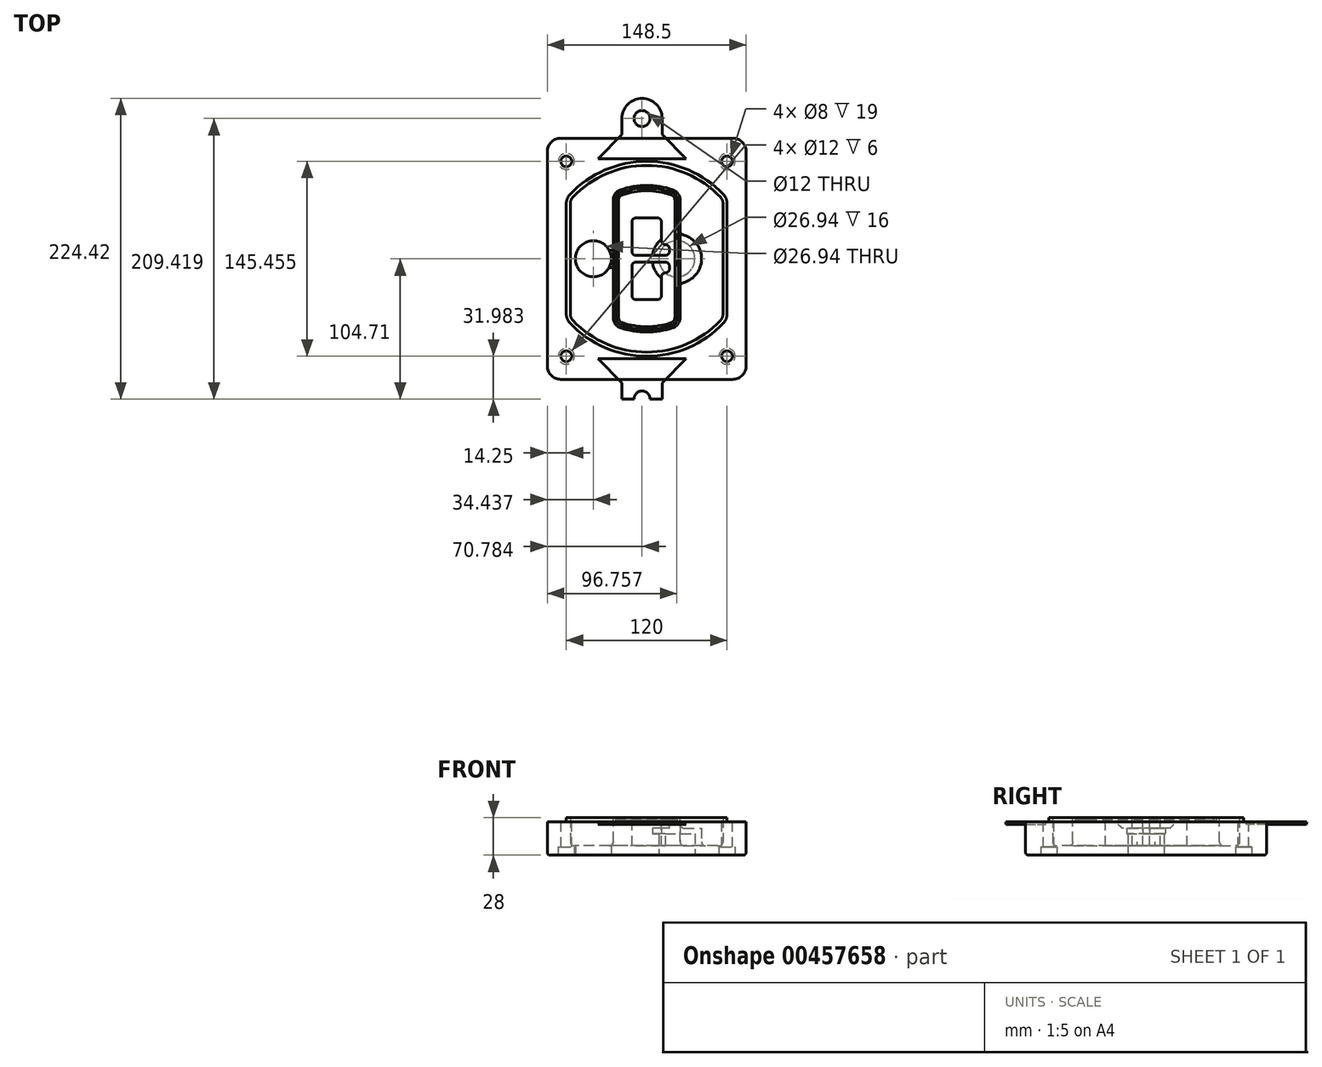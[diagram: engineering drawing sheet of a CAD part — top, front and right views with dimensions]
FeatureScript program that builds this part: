
annotation { "Feature Type Name" : "Feature", "Feature Type Description" : "" }
export const myFeature = defineFeature(function(context is Context, id is Id, definition is map)
    precondition{}
    {
        {
            var Q0;
            Q0=qCreatedBy(makeId("Top.planeOp"),FACE);
            var sketch = newSketch(context, id + "F0", { "sketchPlane" : qUnion([Q0])});
            skPoint(sketch, "E0.rect.middle", {"position": v(0, 0) * mm});
            skLineSegment(sketch, "E1.bottom", {"start": v(-64.25, -90) * mm, "end": v(64.25, -90) * mm});
            skLineSegment(sketch, "E1.top", {"start": v(-64.25, 90) * mm, "end": v(64.25, 90) * mm});
            skLineSegment(sketch, "E1.left", {"start": v(-74.25, -80) * mm, "end": v(-74.25, 80) * mm});
            skLineSegment(sketch, "E1.right", {"start": v(74.25, -80) * mm, "end": v(74.25, 80) * mm});
            skLineSegment(sketch, "E2", {"start": v(-74.25, 90) * mm, "end": v(74.25, -90) * mm, "construction": true});
            skLineSegment(sketch, "E3", {"start": v(74.25, 90) * mm, "end": v(-74.25, -90) * mm, "construction": true});
            skCircle(sketch, "E4", {"center": v(-60, 72.73) * mm, "radius": 4 * mm});
            skCircle(sketch, "E5", {"center": v(60, 72.73) * mm, "radius": 4 * mm});
            skCircle(sketch, "E6", {"center": v(60, -72.73) * mm, "radius": 4 * mm});
            skCircle(sketch, "E7", {"center": v(-60, -72.73) * mm, "radius": 4 * mm});
            skLineSegment(sketch, "E8", {"start": v(-60, 72.73) * mm, "end": v(60, 72.73) * mm, "construction": true});
            skLineSegment(sketch, "E9", {"start": v(60, 72.73) * mm, "end": v(60, -72.73) * mm, "construction": true});
            skLineSegment(sketch, "E10", {"start": v(60, -72.73) * mm, "end": v(-60, -72.73) * mm, "construction": true});
            skLineSegment(sketch, "E11", {"start": v(-60, -72.73) * mm, "end": v(-60, 72.73) * mm, "construction": true});
            skLineSegment(sketch, "E12", {"start": v(-60, 41.18) * mm, "end": v(-60, -41.18) * mm});
            skLineSegment(sketch, "E13", {"start": v(60, 41.18) * mm, "end": v(60, -41.18) * mm});
            skArc(sketch, "E14", {"start": v(57.27, 48.05) * mm, "mid": v(0, 72.73) * mm, "end": v(-57.27, 48.05) * mm});
            skArc(sketch, "E15", {"start": v(-57.27, -48.05) * mm, "mid": v(0, -72.73) * mm, "end": v(57.27, -48.05) * mm});
            skLineSegment(sketch, "E16", {"start": v(-60, 0) * mm, "end": v(60, 0) * mm, "construction": true});
            skPoint(sketch, "E17.visualSharp", {"position": v(-60, -45) * mm});
            skArc(sketch, "E17.filletArc", {"start": v(-60, -41.18) * mm, "mid": v(-59.3, -44.87) * mm, "end": v(-57.27, -48.05) * mm});
            skPoint(sketch, "E18.visualSharp", {"position": v(-60, 45) * mm});
            skArc(sketch, "E18.filletArc", {"start": v(-57.27, 48.05) * mm, "mid": v(-59.3, 44.87) * mm, "end": v(-60, 41.18) * mm});
            skPoint(sketch, "E19.visualSharp", {"position": v(60, 45) * mm});
            skArc(sketch, "E19.filletArc", {"start": v(60, 41.18) * mm, "mid": v(59.3, 44.87) * mm, "end": v(57.27, 48.05) * mm});
            skPoint(sketch, "E20.visualSharp", {"position": v(60, -45) * mm});
            skArc(sketch, "E20.filletArc", {"start": v(57.27, -48.05) * mm, "mid": v(59.3, -44.87) * mm, "end": v(60, -41.18) * mm});
            skPoint(sketch, "E21.visualSharp", {"position": v(-74.25, 90) * mm});
            skArc(sketch, "E21.filletArc", {"start": v(-64.25, 90) * mm, "mid": v(-71.32, 87.07) * mm, "end": v(-74.25, 80) * mm});
            skPoint(sketch, "E22.visualSharp", {"position": v(74.25, 90) * mm});
            skArc(sketch, "E22.filletArc", {"start": v(74.25, 80) * mm, "mid": v(71.32, 87.07) * mm, "end": v(64.25, 90) * mm});
            skPoint(sketch, "E23.visualSharp", {"position": v(74.25, -90) * mm});
            skArc(sketch, "E23.filletArc", {"start": v(64.25, -90) * mm, "mid": v(71.32, -87.07) * mm, "end": v(74.25, -80) * mm});
            skPoint(sketch, "E24.visualSharp", {"position": v(-74.25, -90) * mm});
            skArc(sketch, "E24.filletArc", {"start": v(-74.25, -80) * mm, "mid": v(-71.32, -87.07) * mm, "end": v(-64.25, -90) * mm});
            skArc(sketch, "E25.0", {"start": v(57, 41.18) * mm, "mid": v(56.5, 43.76) * mm, "end": v(55.09, 45.99) * mm});
            skLineSegment(sketch, "E25.1", {"start": v(57, 41.18) * mm, "end": v(57, -41.18) * mm});
            skArc(sketch, "E25.2", {"start": v(55.09, -45.99) * mm, "mid": v(56.5, -43.76) * mm, "end": v(57, -41.18) * mm});
            skArc(sketch, "E25.3", {"start": v(-55.09, -45.99) * mm, "mid": v(0, -69.73) * mm, "end": v(55.09, -45.99) * mm});
            skArc(sketch, "E25.4", {"start": v(-57, -41.18) * mm, "mid": v(-56.5, -43.76) * mm, "end": v(-55.09, -45.99) * mm});
            skArc(sketch, "E25.5", {"start": v(55.09, 45.99) * mm, "mid": v(0, 69.73) * mm, "end": v(-55.09, 45.99) * mm});
            skLineSegment(sketch, "E25.6", {"start": v(-57, 41.18) * mm, "end": v(-57, -41.18) * mm});
            skArc(sketch, "E25.7", {"start": v(-55.09, 45.99) * mm, "mid": v(-56.5, 43.76) * mm, "end": v(-57, 41.18) * mm});
            skArc(sketch, "E26.0", {"start": v(-60.18, 50.8) * mm, "mid": v(-63, 46.35) * mm, "end": v(-64, 41.18) * mm});
            skArc(sketch, "E26.1", {"start": v(60.18, 50.8) * mm, "mid": v(0, 76.73) * mm, "end": v(-60.18, 50.8) * mm});
            skArc(sketch, "E26.2", {"start": v(64, 41.18) * mm, "mid": v(63, 46.35) * mm, "end": v(60.18, 50.8) * mm});
            skLineSegment(sketch, "E26.3", {"start": v(64, 41.18) * mm, "end": v(64, -41.18) * mm});
            skArc(sketch, "E26.4", {"start": v(60.18, -50.8) * mm, "mid": v(63, -46.35) * mm, "end": v(64, -41.18) * mm});
            skLineSegment(sketch, "E26.5", {"start": v(-64, 41.18) * mm, "end": v(-64, -41.18) * mm});
            skArc(sketch, "E26.6", {"start": v(-60.18, -50.8) * mm, "mid": v(0, -76.73) * mm, "end": v(60.18, -50.8) * mm});
            skArc(sketch, "E26.7", {"start": v(-64, -41.18) * mm, "mid": v(-63, -46.35) * mm, "end": v(-60.18, -50.8) * mm});
            skSolve(sketch);
        }
        {
            var Q0;
            Q0=makeQuery(id+"F0.imprint","IMPRINT",FACE,{"disambiguationData":[TD([[makeQuery(id+"F0.imprint","IMPRINT",EDGE,{"derivedFrom":sQuery(id+"F0.wireOp",EDGE,"E1.bottom")}),1.0]])]});
            var Q1;
            Q1=makeQuery(id+"F0.imprint","IMPRINT",FACE,{"disambiguationData":[TD([[makeQuery(id+"F0.imprint","IMPRINT",EDGE,{"derivedFrom":sQuery(id+"F0.wireOp",EDGE,"E12")}),1.0]])]});
            var Q2;
            Q2=makeQuery(id+"F0.imprint","IMPRINT",FACE,{"disambiguationData":[TD([[makeQuery(id+"F0.imprint","IMPRINT",EDGE,{"derivedFrom":sQuery(id+"F0.wireOp",EDGE,"E25.0")}),1.0]])]});
            var Q3;
            Q3=makeQuery(id+"F0.imprint","IMPRINT",FACE,{"disambiguationData":[TD([[makeQuery(id+"F0.imprint","IMPRINT",EDGE,{"derivedFrom":sQuery(id+"F0.wireOp",EDGE,"E12")}),-1.0]])]});
            extrude(context, id + "F1", {"entities" : qUnion([Q0, Q1, Q2, Q3]), "oppositeDirection" : true, "depth" : 25 * mm});
        }
        {
            var Q0;
            Q0=makeQuery(id+"F0.imprint","IMPRINT",FACE,{"disambiguationData":[TD([[makeQuery(id+"F0.imprint","IMPRINT",EDGE,{"derivedFrom":sQuery(id+"F0.wireOp",EDGE,"E12")}),1.0]])]});
            extrude(context, id + "F2", {"entities" : qUnion([Q0]), "operationType" : NewBodyOperationType.ADD, "depth" : 3 * mm});
        }
        {
            var Q0;
            Q0=makeQuery(id+"F0.imprint","IMPRINT",FACE,{"disambiguationData":[TD([[makeQuery(id+"F0.imprint","IMPRINT",EDGE,{"derivedFrom":sQuery(id+"F0.wireOp",EDGE,"E25.0")}),1.0]])]});
            extrude(context, id + "F3", {"entities" : qUnion([Q0]), "operationType" : NewBodyOperationType.REMOVE, "oppositeDirection" : true, "depth" : 18 * mm});
        }
        {
            var Q0;
            Q0=makeQuery(id+"F2.opExtrude","CAP_FACE",FACE,{"disambiguationData":[OSD([sQuery(id+"F0.wireOp",EDGE,"E12"),sQuery(id+"F0.wireOp",EDGE,"E13"),sQuery(id+"F0.wireOp",EDGE,"E14"),sQuery(id+"F0.wireOp",EDGE,"E15"),sQuery(id+"F0.wireOp",EDGE,"E17.filletArc"),sQuery(id+"F0.wireOp",EDGE,"E18.filletArc"),sQuery(id+"F0.wireOp",EDGE,"E19.filletArc"),sQuery(id+"F0.wireOp",EDGE,"E20.filletArc"),sQuery(id+"F0.wireOp",EDGE,"E25.0"),sQuery(id+"F0.wireOp",EDGE,"E25.1"),sQuery(id+"F0.wireOp",EDGE,"E25.2"),sQuery(id+"F0.wireOp",EDGE,"E25.3"),sQuery(id+"F0.wireOp",EDGE,"E25.4"),sQuery(id+"F0.wireOp",EDGE,"E25.5"),sQuery(id+"F0.wireOp",EDGE,"E25.6"),sQuery(id+"F0.wireOp",EDGE,"E25.7")])],"isStart":false});
            var sketch = newSketch(context, id + "F4", { "sketchPlane" : qUnion([Q0])});
            skArc(sketch, "E27.0", {"start": v(-19.58, -51.49) * mm, "mid": v(0, -54.73) * mm, "end": v(19.58, -51.49) * mm});
            skArc(sketch, "E28.0", {"start": v(19.58, 51.49) * mm, "mid": v(0, 54.73) * mm, "end": v(-19.58, 51.49) * mm});
            skLineSegment(sketch, "E29", {"start": v(-25, 43.91) * mm, "end": v(-25, -43.91) * mm});
            skLineSegment(sketch, "E30", {"start": v(25, 43.91) * mm, "end": v(25, -43.91) * mm});
            skLineSegment(sketch, "E31", {"start": v(-25, 49.35) * mm, "end": v(25, 49.35) * mm, "construction": true});
            skLineSegment(sketch, "E32", {"start": v(-25, -49.35) * mm, "end": v(25, -49.35) * mm, "construction": true});
            skPoint(sketch, "E33.visualSharp", {"position": v(-25, 49.35) * mm});
            skArc(sketch, "E33.filletArc", {"start": v(-19.58, 51.49) * mm, "mid": v(-23.5, 48.57) * mm, "end": v(-25, 43.91) * mm});
            skPoint(sketch, "E34.visualSharp", {"position": v(25, 49.35) * mm});
            skArc(sketch, "E34.filletArc", {"start": v(25, 43.91) * mm, "mid": v(23.5, 48.57) * mm, "end": v(19.58, 51.49) * mm});
            skPoint(sketch, "E35.visualSharp", {"position": v(25, -49.35) * mm});
            skArc(sketch, "E35.filletArc", {"start": v(19.58, -51.49) * mm, "mid": v(23.5, -48.57) * mm, "end": v(25, -43.91) * mm});
            skPoint(sketch, "E36.visualSharp", {"position": v(-25, -49.35) * mm});
            skArc(sketch, "E36.filletArc", {"start": v(-25, -43.91) * mm, "mid": v(-23.5, -48.57) * mm, "end": v(-19.58, -51.49) * mm});
            skArc(sketch, "E37.0", {"start": v(55.09, 45.99) * mm, "mid": v(0, 69.73) * mm, "end": v(-55.09, 45.99) * mm});
            skArc(sketch, "E37.1", {"start": v(-55.09, 45.99) * mm, "mid": v(-56.5, 43.76) * mm, "end": v(-57, 41.18) * mm});
            skLineSegment(sketch, "E37.2", {"start": v(-57, 41.18) * mm, "end": v(-57, -41.18) * mm});
            skArc(sketch, "E37.3", {"start": v(-57, -41.18) * mm, "mid": v(-56.5, -43.76) * mm, "end": v(-55.09, -45.99) * mm});
            skArc(sketch, "E37.4", {"start": v(-55.09, -45.99) * mm, "mid": v(0, -69.73) * mm, "end": v(55.09, -45.99) * mm});
            skArc(sketch, "E37.5", {"start": v(55.09, -45.99) * mm, "mid": v(56.5, -43.76) * mm, "end": v(57, -41.18) * mm});
            skLineSegment(sketch, "E37.6", {"start": v(57, 41.18) * mm, "end": v(57, -41.18) * mm});
            skArc(sketch, "E37.7", {"start": v(57, 41.18) * mm, "mid": v(56.5, 43.76) * mm, "end": v(55.09, 45.99) * mm});
            skLineSegment(sketch, "E38.0", {"start": v(23, 43.91) * mm, "end": v(23, -43.91) * mm});
            skArc(sketch, "E38.1", {"start": v(18.93, -49.6) * mm, "mid": v(21.88, -47.4) * mm, "end": v(23, -43.91) * mm});
            skArc(sketch, "E38.2", {"start": v(-18.93, -49.6) * mm, "mid": v(0, -52.73) * mm, "end": v(18.93, -49.6) * mm});
            skArc(sketch, "E38.3", {"start": v(-23, -43.91) * mm, "mid": v(-21.88, -47.4) * mm, "end": v(-18.93, -49.6) * mm});
            skLineSegment(sketch, "E38.4", {"start": v(-23, 43.91) * mm, "end": v(-23, -43.91) * mm});
            skArc(sketch, "E38.5", {"start": v(23, 43.91) * mm, "mid": v(21.88, 47.4) * mm, "end": v(18.93, 49.6) * mm});
            skArc(sketch, "E38.6", {"start": v(-18.93, 49.6) * mm, "mid": v(-21.88, 47.4) * mm, "end": v(-23, 43.91) * mm});
            skArc(sketch, "E38.7", {"start": v(18.93, 49.6) * mm, "mid": v(0, 52.73) * mm, "end": v(-18.93, 49.6) * mm});
            skArc(sketch, "E39.0", {"start": v(21, 43.91) * mm, "mid": v(20.25, 46.24) * mm, "end": v(18.29, 47.7) * mm});
            skLineSegment(sketch, "E39.1", {"start": v(21, 43.91) * mm, "end": v(21, -43.91) * mm});
            skArc(sketch, "E39.2", {"start": v(18.29, -47.7) * mm, "mid": v(20.25, -46.24) * mm, "end": v(21, -43.91) * mm});
            skArc(sketch, "E39.3", {"start": v(-18.29, -47.7) * mm, "mid": v(0, -50.73) * mm, "end": v(18.29, -47.7) * mm});
            skArc(sketch, "E39.4", {"start": v(-21, -43.91) * mm, "mid": v(-20.25, -46.24) * mm, "end": v(-18.29, -47.7) * mm});
            skArc(sketch, "E39.5", {"start": v(18.29, 47.7) * mm, "mid": v(0, 50.73) * mm, "end": v(-18.29, 47.7) * mm});
            skLineSegment(sketch, "E39.6", {"start": v(-21, 43.91) * mm, "end": v(-21, -43.91) * mm});
            skArc(sketch, "E39.7", {"start": v(-18.29, 47.7) * mm, "mid": v(-20.25, 46.24) * mm, "end": v(-21, 43.91) * mm});
            skLineSegment(sketch, "E40", {"start": v(-25, 0) * mm, "end": v(25, 0) * mm, "construction": true});
            skLineSegment(sketch, "E41", {"start": v(-11, 5.5) * mm, "end": v(-11, 27.5) * mm});
            skLineSegment(sketch, "E42", {"start": v(-8, 30.5) * mm, "end": v(8, 30.5) * mm});
            skLineSegment(sketch, "E43", {"start": v(11, 27.5) * mm, "end": v(11, 13.5) * mm});
            skLineSegment(sketch, "E44", {"start": v(14, 10.5) * mm, "end": v(14, 10.5) * mm});
            skLineSegment(sketch, "E45", {"start": v(17, 7.5) * mm, "end": v(17, 5.5) * mm});
            skLineSegment(sketch, "E46", {"start": v(14, 2.5) * mm, "end": v(-8, 2.5) * mm});
            skPoint(sketch, "E47.visualSharp", {"position": v(-11, 30.5) * mm});
            skArc(sketch, "E47.filletArc", {"start": v(-8, 30.5) * mm, "mid": v(-10.12, 29.62) * mm, "end": v(-11, 27.5) * mm});
            skPoint(sketch, "E48.visualSharp", {"position": v(11, 30.5) * mm});
            skArc(sketch, "E48.filletArc", {"start": v(11, 27.5) * mm, "mid": v(10.12, 29.62) * mm, "end": v(8, 30.5) * mm});
            skPoint(sketch, "E49.visualSharp", {"position": v(11, 10.5) * mm});
            skArc(sketch, "E49.filletArc", {"start": v(11, 13.5) * mm, "mid": v(11.88, 11.38) * mm, "end": v(14, 10.5) * mm});
            skPoint(sketch, "E50.visualSharp", {"position": v(17, 10.5) * mm});
            skArc(sketch, "E50.filletArc", {"start": v(17, 7.5) * mm, "mid": v(16.12, 9.62) * mm, "end": v(14, 10.5) * mm});
            skPoint(sketch, "E51.visualSharp", {"position": v(17, 2.5) * mm});
            skArc(sketch, "E51.filletArc", {"start": v(14, 2.5) * mm, "mid": v(16.12, 3.38) * mm, "end": v(17, 5.5) * mm});
            skPoint(sketch, "E52.visualSharp", {"position": v(-11, 2.5) * mm});
            skArc(sketch, "E52.filletArc", {"start": v(-11, 5.5) * mm, "mid": v(-10.12, 3.38) * mm, "end": v(-8, 2.5) * mm});
            skLineSegment(sketch, "E53.0.MirrorCS", {"start": v(14, -2.5) * mm, "end": v(-8, -2.5) * mm});
            skArc(sketch, "E54.0.MirrorCS", {"start": v(-11, -5.5) * mm, "mid": v(-10.12, -3.38) * mm, "end": v(-8, -2.5) * mm});
            skLineSegment(sketch, "E55.0.MirrorCS", {"start": v(-11, -5.5) * mm, "end": v(-11, -27.5) * mm});
            skArc(sketch, "E56.0.MirrorCS", {"start": v(-8, -30.5) * mm, "mid": v(-10.12, -29.62) * mm, "end": v(-11, -27.5) * mm});
            skLineSegment(sketch, "E57.0.MirrorCS", {"start": v(-8, -30.5) * mm, "end": v(8, -30.5) * mm});
            skArc(sketch, "E58.0.MirrorCS", {"start": v(11, -27.5) * mm, "mid": v(10.12, -29.62) * mm, "end": v(8, -30.5) * mm});
            skLineSegment(sketch, "E59.0.MirrorCS", {"start": v(11, -27.5) * mm, "end": v(11, -13.5) * mm});
            skArc(sketch, "E60.0.MirrorCS", {"start": v(11, -13.5) * mm, "mid": v(11.88, -11.38) * mm, "end": v(14, -10.5) * mm});
            skArc(sketch, "E61.0.MirrorCS", {"start": v(17, -7.5) * mm, "mid": v(16.12, -9.62) * mm, "end": v(14, -10.5) * mm});
            skLineSegment(sketch, "E62.0.MirrorCS", {"start": v(17, -7.5) * mm, "end": v(17, -5.5) * mm});
            skArc(sketch, "E63.0.MirrorCS", {"start": v(14, -2.5) * mm, "mid": v(16.12, -3.38) * mm, "end": v(17, -5.5) * mm});
            skSolve(sketch);
        }
        {
            var Q0;
            Q0=makeQuery(id+"F4.imprint","IMPRINT",FACE,{"disambiguationData":[TD([[makeQuery(id+"F4.imprint","IMPRINT",EDGE,{"derivedFrom":sQuery(id+"F4.wireOp",EDGE,"E27.0")}),1.0]])]});
            var Q1;
            Q1=makeQuery(id+"F4.imprint","IMPRINT",FACE,{"disambiguationData":[TD([[makeQuery(id+"F4.imprint","IMPRINT",EDGE,{"derivedFrom":sQuery(id+"F4.wireOp",EDGE,"E38.0")}),-1.0]])]});
            var Q2;
            Q2=makeQuery(id+"F4.imprint","IMPRINT",FACE,{"disambiguationData":[TD([[makeQuery(id+"F4.imprint","IMPRINT",EDGE,{"derivedFrom":sQuery(id+"F4.wireOp",EDGE,"E39.0")}),1.0]])]});
            extrude(context, id + "F5", {"entities" : qUnion([Q0, Q1, Q2]), "operationType" : NewBodyOperationType.ADD, "endBound" : BoundingType.UP_TO_NEXT, "oppositeDirection" : true, "depth" : 25 * mm});
        }
        {
            var Q0;
            Q0=makeQuery(id+"F4.imprint","IMPRINT",FACE,{"disambiguationData":[TD([[makeQuery(id+"F4.imprint","IMPRINT",EDGE,{"derivedFrom":sQuery(id+"F4.wireOp",EDGE,"E38.0")}),-1.0]])]});
            extrude(context, id + "F6", {"entities" : qUnion([Q0]), "operationType" : NewBodyOperationType.REMOVE, "oppositeDirection" : true, "depth" : 2 * mm});
        }
        {
            var Q0;
            Q0=makeQuery(id+"F1.opExtrude","CAP_FACE",FACE,{"disambiguationData":[OSD([sQuery(id+"F0.wireOp",EDGE,"E1.bottom"),sQuery(id+"F0.wireOp",EDGE,"E1.top"),sQuery(id+"F0.wireOp",EDGE,"E1.left"),sQuery(id+"F0.wireOp",EDGE,"E1.right"),sQuery(id+"F0.wireOp",EDGE,"E4"),sQuery(id+"F0.wireOp",EDGE,"E5"),sQuery(id+"F0.wireOp",EDGE,"E6"),sQuery(id+"F0.wireOp",EDGE,"E7"),sQuery(id+"F0.wireOp",EDGE,"E21.filletArc"),sQuery(id+"F0.wireOp",EDGE,"E22.filletArc"),sQuery(id+"F0.wireOp",EDGE,"E23.filletArc"),sQuery(id+"F0.wireOp",EDGE,"E24.filletArc")])],"isStart":false});
            var sketch = newSketch(context, id + "F7", { "sketchPlane" : qUnion([Q0])});
            skCircle(sketch, "E64", {"center": v(22.5, 0) * mm, "radius": 13.47 * mm});
            skCircle(sketch, "E65", {"center": v(-39.81, 0) * mm, "radius": 13.47 * mm});
            skLineSegment(sketch, "E66", {"start": v(74.25, 0) * mm, "end": v(-74.25, 0) * mm});
            skCircle(sketch, "E67", {"center": v(22.5, 0) * mm, "radius": 18.47 * mm});
            skCircle(sketch, "E68", {"center": v(60, -72.73) * mm, "radius": 6 * mm});
            skCircle(sketch, "E69", {"center": v(-60, -72.73) * mm, "radius": 6 * mm});
            skCircle(sketch, "E70", {"center": v(-60, 72.73) * mm, "radius": 6 * mm});
            skCircle(sketch, "E71", {"center": v(60, 72.73) * mm, "radius": 6 * mm});
            skSolve(sketch);
        }
        {
            var Q0;
            {var subQ1=sQuery(id+"F7.wireOp",EDGE,"E66");var subQ4=sQuery(id+"F7.wireOp",EDGE,"E64");var subQ6=makeQuery(id+"F7.imprint","INTERSECT",VERTEX,{"disambiguationData":[OD(0.0)],"derivedFrom":[subQ4,subQ1]});Q0=makeQuery(id+"F7.imprint","IMPRINT",FACE,{"disambiguationData":[TD([[makeQuery(id+"F7.imprint","IMPRINT",EDGE,{"disambiguationData":[TD([[subQ6,-1.0]])],"derivedFrom":subQ4}),-1.0]])]});}
            var Q1;
            {var subQ0=sQuery(id+"F7.wireOp",EDGE,"E66");var subQ1=sQuery(id+"F7.wireOp",EDGE,"E64");var subQ3=makeQuery(id+"F7.imprint","INTERSECT",VERTEX,{"disambiguationData":[OD(0.0)],"derivedFrom":[subQ1,subQ0]});Q1=makeQuery(id+"F7.imprint","IMPRINT",FACE,{"disambiguationData":[TD([[makeQuery(id+"F7.imprint","IMPRINT",EDGE,{"disambiguationData":[TD([[subQ3,-1.0]])],"derivedFrom":subQ1}),1.0]])]});}
            var Q2;
            {var subQ0=sQuery(id+"F7.wireOp",EDGE,"E66");var subQ1=sQuery(id+"F7.wireOp",EDGE,"E64");var subQ3=makeQuery(id+"F7.imprint","INTERSECT",VERTEX,{"disambiguationData":[OD(0.0)],"derivedFrom":[subQ1,subQ0]});Q2=makeQuery(id+"F7.imprint","IMPRINT",FACE,{"disambiguationData":[TD([[makeQuery(id+"F7.imprint","IMPRINT",EDGE,{"disambiguationData":[TD([[subQ3,1.0]])],"derivedFrom":subQ1}),1.0]])]});}
            var Q3;
            {var subQ1=sQuery(id+"F7.wireOp",EDGE,"E66");var subQ4=sQuery(id+"F7.wireOp",EDGE,"E64");var subQ6=makeQuery(id+"F7.imprint","INTERSECT",VERTEX,{"disambiguationData":[OD(0.0)],"derivedFrom":[subQ4,subQ1]});Q3=makeQuery(id+"F7.imprint","IMPRINT",FACE,{"disambiguationData":[TD([[makeQuery(id+"F7.imprint","IMPRINT",EDGE,{"disambiguationData":[TD([[subQ6,1.0]])],"derivedFrom":subQ4}),-1.0]])]});}
            extrude(context, id + "F8", {"entities" : qUnion([Q0, Q1, Q2, Q3]), "operationType" : NewBodyOperationType.ADD, "oppositeDirection" : true, "depth" : 20 * mm});
        }
        {
            var Q0;
            {var subQ0=sQuery(id+"F7.wireOp",EDGE,"E66");var subQ1=sQuery(id+"F7.wireOp",EDGE,"E64");var subQ3=makeQuery(id+"F7.imprint","INTERSECT",VERTEX,{"disambiguationData":[OD(0.0)],"derivedFrom":[subQ1,subQ0]});Q0=makeQuery(id+"F7.imprint","IMPRINT",FACE,{"disambiguationData":[TD([[makeQuery(id+"F7.imprint","IMPRINT",EDGE,{"disambiguationData":[TD([[subQ3,-1.0]])],"derivedFrom":subQ1}),1.0]])]});}
            var Q1;
            {var subQ0=sQuery(id+"F7.wireOp",EDGE,"E66");var subQ1=sQuery(id+"F7.wireOp",EDGE,"E64");var subQ3=makeQuery(id+"F7.imprint","INTERSECT",VERTEX,{"disambiguationData":[OD(0.0)],"derivedFrom":[subQ1,subQ0]});Q1=makeQuery(id+"F7.imprint","IMPRINT",FACE,{"disambiguationData":[TD([[makeQuery(id+"F7.imprint","IMPRINT",EDGE,{"disambiguationData":[TD([[subQ3,1.0]])],"derivedFrom":subQ1}),1.0]])]});}
            extrude(context, id + "F9", {"entities" : qUnion([Q0, Q1]), "operationType" : NewBodyOperationType.REMOVE, "oppositeDirection" : true, "depth" : 16 * mm});
        }
        {
            var Q0;
            {var subQ0=sQuery(id+"F7.wireOp",EDGE,"E66");var subQ1=sQuery(id+"F7.wireOp",EDGE,"E65");var subQ3=makeQuery(id+"F7.imprint","INTERSECT",VERTEX,{"disambiguationData":[OD(0.0)],"derivedFrom":[subQ1,subQ0]});Q0=makeQuery(id+"F7.imprint","IMPRINT",FACE,{"disambiguationData":[TD([[makeQuery(id+"F7.imprint","IMPRINT",EDGE,{"disambiguationData":[TD([[subQ3,-1.0]])],"derivedFrom":subQ1}),1.0]])]});}
            var Q1;
            {var subQ0=sQuery(id+"F7.wireOp",EDGE,"E66");var subQ1=sQuery(id+"F7.wireOp",EDGE,"E65");var subQ3=makeQuery(id+"F7.imprint","INTERSECT",VERTEX,{"disambiguationData":[OD(0.0)],"derivedFrom":[subQ1,subQ0]});Q1=makeQuery(id+"F7.imprint","IMPRINT",FACE,{"disambiguationData":[TD([[makeQuery(id+"F7.imprint","IMPRINT",EDGE,{"disambiguationData":[TD([[subQ3,1.0]])],"derivedFrom":subQ1}),1.0]])]});}
            extrude(context, id + "F10", {"entities" : qUnion([Q0, Q1]), "operationType" : NewBodyOperationType.REMOVE, "oppositeDirection" : true, "depth" : 25 * mm});
        }
        {
            var Q0;
            Q0=makeQuery(id+"F7.imprint","IMPRINT",FACE,{"disambiguationData":[TD([[makeQuery(id+"F7.imprint","IMPRINT",EDGE,{"derivedFrom":sQuery(id+"F7.wireOp",EDGE,"E68")}),1.0]])]});
            var Q1;
            Q1=makeQuery(id+"F7.imprint","IMPRINT",FACE,{"disambiguationData":[TD([[makeQuery(id+"F7.imprint","IMPRINT",EDGE,{"derivedFrom":makeQuery(id+"F1.opExtrude","CAP_EDGE",EDGE,{"disambiguationData":[OSD([sQuery(id+"F0.wireOp",EDGE,"E5")])],"isStart":false})}),-1.0]])]});
            var Q2;
            Q2=makeQuery(id+"F7.imprint","IMPRINT",FACE,{"disambiguationData":[TD([[makeQuery(id+"F7.imprint","IMPRINT",EDGE,{"derivedFrom":sQuery(id+"F7.wireOp",EDGE,"E69")}),1.0]])]});
            var Q3;
            Q3=makeQuery(id+"F7.imprint","IMPRINT",FACE,{"disambiguationData":[TD([[makeQuery(id+"F7.imprint","IMPRINT",EDGE,{"derivedFrom":makeQuery(id+"F1.opExtrude","CAP_EDGE",EDGE,{"disambiguationData":[OSD([sQuery(id+"F0.wireOp",EDGE,"E4")])],"isStart":false})}),-1.0]])]});
            var Q4;
            Q4=makeQuery(id+"F7.imprint","IMPRINT",FACE,{"disambiguationData":[TD([[makeQuery(id+"F7.imprint","IMPRINT",EDGE,{"derivedFrom":sQuery(id+"F7.wireOp",EDGE,"E70")}),1.0]])]});
            var Q5;
            Q5=makeQuery(id+"F7.imprint","IMPRINT",FACE,{"disambiguationData":[TD([[makeQuery(id+"F7.imprint","IMPRINT",EDGE,{"derivedFrom":makeQuery(id+"F1.opExtrude","CAP_EDGE",EDGE,{"disambiguationData":[OSD([sQuery(id+"F0.wireOp",EDGE,"E7")])],"isStart":false})}),-1.0]])]});
            var Q6;
            Q6=makeQuery(id+"F7.imprint","IMPRINT",FACE,{"disambiguationData":[TD([[makeQuery(id+"F7.imprint","IMPRINT",EDGE,{"derivedFrom":sQuery(id+"F7.wireOp",EDGE,"E71")}),1.0]])]});
            var Q7;
            Q7=makeQuery(id+"F7.imprint","IMPRINT",FACE,{"disambiguationData":[TD([[makeQuery(id+"F7.imprint","IMPRINT",EDGE,{"derivedFrom":makeQuery(id+"F1.opExtrude","CAP_EDGE",EDGE,{"disambiguationData":[OSD([sQuery(id+"F0.wireOp",EDGE,"E6")])],"isStart":false})}),-1.0]])]});
            extrude(context, id + "F11", {"entities" : qUnion([Q0, Q1, Q2, Q3, Q4, Q5, Q6, Q7]), "operationType" : NewBodyOperationType.REMOVE, "oppositeDirection" : true, "depth" : 6 * mm});
        }
        {
            var Q0;
            Q0=makeQuery(id+"F9.boolean.opBoolean","COPY",FACE,{"derivedFrom":makeQuery(id+"F9.opExtrude","CAP_FACE",FACE,{"disambiguationData":[OSD([sQuery(id+"F7.wireOp",EDGE,"E64")])],"isStart":false})});
            var sketch = newSketch(context, id + "F12", { "sketchPlane" : qUnion([Q0])});
            skArc(sketch, "E72.0", {"start": v(11, 14.45) * mm, "mid": v(6.45, 9.13) * mm, "end": v(4.2, 2.5) * mm});
            skArc(sketch, "E72.1", {"start": v(4.2, -2.5) * mm, "mid": v(6.45, -9.13) * mm, "end": v(11, -14.45) * mm});
            skLineSegment(sketch, "E73", {"start": v(4.2, -2.5) * mm, "end": v(14, -2.5) * mm});
            skLineSegment(sketch, "E74.0", {"start": v(14, 2.5) * mm, "end": v(4.2, 2.5) * mm});
            skArc(sketch, "E74.1", {"start": v(14, 2.5) * mm, "mid": v(16.12, 3.38) * mm, "end": v(17, 5.5) * mm});
            skLineSegment(sketch, "E74.2", {"start": v(17, 7.5) * mm, "end": v(17, 5.5) * mm});
            skArc(sketch, "E74.3", {"start": v(17, 7.5) * mm, "mid": v(16.12, 9.62) * mm, "end": v(14, 10.5) * mm});
            skArc(sketch, "E74.4", {"start": v(11, 13.5) * mm, "mid": v(11.88, 11.38) * mm, "end": v(14, 10.5) * mm});
            skLineSegment(sketch, "E74.5", {"start": v(11, 14.45) * mm, "end": v(11, 13.5) * mm});
            skLineSegment(sketch, "E74.7", {"start": v(14, -2.5) * mm, "end": v(4.2, -2.5) * mm});
            skArc(sketch, "E74.8", {"start": v(14, -2.5) * mm, "mid": v(16.12, -3.38) * mm, "end": v(17, -5.5) * mm});
            skLineSegment(sketch, "E74.9", {"start": v(17, -7.5) * mm, "end": v(17, -5.5) * mm});
            skArc(sketch, "E74.10", {"start": v(17, -7.5) * mm, "mid": v(16.12, -9.62) * mm, "end": v(14, -10.5) * mm});
            skArc(sketch, "E74.11", {"start": v(11, -13.5) * mm, "mid": v(11.88, -11.38) * mm, "end": v(14, -10.5) * mm});
            skLineSegment(sketch, "E74.12", {"start": v(11, -14.45) * mm, "end": v(11, -13.5) * mm});
            skPoint(sketch, "E75.orphan", {"position": v(11, -27.5) * mm});
            skPoint(sketch, "E76.orphan", {"position": v(-8, -2.5) * mm});
            skPoint(sketch, "E77.orphan", {"position": v(-8, 2.5) * mm});
            skPoint(sketch, "E78.orphan", {"position": v(11, 27.5) * mm});
            skSolve(sketch);
        }
        {
            var Q0;
            {var subQ7=sQuery(id+"F12.wireOp",EDGE,"E72.0");var subQ14=sQuery(id+"F12.wireOp",EDGE,"E72.1");var subQ16=sQuery(id+"F12.wireOp",EDGE,"E74.1");var subQ18=sQuery(id+"F12.wireOp",EDGE,"E74.8");Q0=qUnion([makeQuery(id+"F12.imprint","IMPRINT",FACE,{"disambiguationData":[TD([[makeQuery(id+"F12.imprint","IMPRINT",EDGE,{"derivedFrom":subQ7}),1.0]])]}),makeQuery(id+"F12.imprint","IMPRINT",FACE,{"disambiguationData":[TD([[makeQuery(id+"F12.imprint","IMPRINT",EDGE,{"derivedFrom":subQ14}),1.0]])]}),makeQuery(id+"F12.imprint","IMPRINT",FACE,{"disambiguationData":[TD([[makeQuery(id+"F12.imprint","IMPRINT",EDGE,{"derivedFrom":subQ16}),1.0]])]}),makeQuery(id+"F12.imprint","IMPRINT",FACE,{"disambiguationData":[TD([[makeQuery(id+"F12.imprint","IMPRINT",EDGE,{"derivedFrom":subQ18}),-1.0]])]})]);}
            var Q1;
            Q1=makeQuery(id+"F5.boolean.opBoolean","SPLIT",FACE,{"disambiguationData":[TD([makeQuery(id+"F5.opExtrude","SWEPT_FACE",FACE,{"disambiguationData":[OSD([sQuery(id+"F4.wireOp",EDGE,"E41")])]})])],"derivedFrom":makeQuery(id+"F3.boolean.opBoolean","COPY",FACE,{"derivedFrom":makeQuery(id+"F3.opExtrude","CAP_FACE",FACE,{"disambiguationData":[OSD([sQuery(id+"F0.wireOp",EDGE,"E25.0"),sQuery(id+"F0.wireOp",EDGE,"E25.1"),sQuery(id+"F0.wireOp",EDGE,"E25.2"),sQuery(id+"F0.wireOp",EDGE,"E25.3"),sQuery(id+"F0.wireOp",EDGE,"E25.4"),sQuery(id+"F0.wireOp",EDGE,"E25.5"),sQuery(id+"F0.wireOp",EDGE,"E25.6"),sQuery(id+"F0.wireOp",EDGE,"E25.7")])],"isStart":false})})});
            extrude(context, id + "F13", {"entities" : qUnion([Q0]), "operationType" : NewBodyOperationType.REMOVE, "endBound" : BoundingType.UP_TO_SURFACE, "endBoundEntityFace" : qUnion([Q1]), "depth" : 25 * mm});
        }
        {
            var Q0;
            Q0=makeQuery(id+"F3.boolean.opBoolean","COPY",EDGE,{"derivedFrom":makeQuery(id+"F3.opExtrude","CAP_EDGE",EDGE,{"disambiguationData":[OSD([sQuery(id+"F0.wireOp",EDGE,"E25.6")])],"isStart":false})});
            var Q1;
            Q1=makeQuery(id+"F8.boolean.opBoolean","INTERSECT",EDGE,{"derivedFrom":[makeQuery(id+"F5.opExtrude","SWEPT_FACE",FACE,{"disambiguationData":[OSD([sQuery(id+"F4.wireOp",EDGE,"E30")])]}),makeQuery(id+"F8.opExtrude","CAP_FACE",FACE,{"disambiguationData":[OSD([sQuery(id+"F7.wireOp",EDGE,"E67")])],"isStart":false})]});
            var Q2;
            Q2=makeQuery(id+"F8.boolean.opBoolean","INTERSECT",EDGE,{"disambiguationData":[OD(1.0)],"derivedFrom":[makeQuery(id+"F5.opExtrude","SWEPT_FACE",FACE,{"disambiguationData":[OSD([sQuery(id+"F4.wireOp",EDGE,"E30")])]}),makeQuery(id+"F8.opExtrude","SWEPT_FACE",FACE,{"disambiguationData":[OSD([sQuery(id+"F7.wireOp",EDGE,"E67")])]})]});
            var Q3;
            {var subQ0=sQuery(id+"F4.wireOp",EDGE,"E30");Q3=makeQuery(id+"F8.boolean.opBoolean","SPLIT",EDGE,{"disambiguationData":[TD([makeQuery(id+"F5.opExtrude","SWEPT_FACE",FACE,{"disambiguationData":[OSD([sQuery(id+"F4.wireOp",EDGE,"E35.filletArc")])]})])],"derivedFrom":makeQuery(id+"F5.opExtrude","CAP_EDGE",EDGE,{"disambiguationData":[OSD([subQ0])],"isStart":false})});}
            var Q4;
            {var subQ0=sQuery(id+"F0.wireOp",EDGE,"E25.7");var subQ1=sQuery(id+"F0.wireOp",EDGE,"E25.1");var subQ2=sQuery(id+"F0.wireOp",EDGE,"E25.6");var subQ3=sQuery(id+"F0.wireOp",EDGE,"E25.5");var subQ4=sQuery(id+"F0.wireOp",EDGE,"E25.4");var subQ5=sQuery(id+"F0.wireOp",EDGE,"E25.0");var subQ6=sQuery(id+"F0.wireOp",EDGE,"E25.2");var subQ7=sQuery(id+"F0.wireOp",EDGE,"E25.3");Q4=makeQuery(id+"F8.boolean.opBoolean","INTERSECT",EDGE,{"derivedFrom":[makeQuery(id+"F5.boolean.opBoolean","SPLIT",FACE,{"disambiguationData":[TD([makeQuery(id+"F2.opExtrude","SWEPT_FACE",FACE,{"disambiguationData":[OSD([subQ5])]})])],"derivedFrom":makeQuery(id+"F3.boolean.opBoolean","COPY",FACE,{"derivedFrom":makeQuery(id+"F3.opExtrude","CAP_FACE",FACE,{"disambiguationData":[OSD([subQ5,subQ1,subQ6,subQ7,subQ4,subQ3,subQ2,subQ0])],"isStart":false})})}),makeQuery(id+"F8.opExtrude","SWEPT_FACE",FACE,{"disambiguationData":[OSD([sQuery(id+"F7.wireOp",EDGE,"E67")])]})]});}
            var Q5;
            Q5=makeQuery(id+"F8.boolean.opBoolean","INTERSECT",EDGE,{"disambiguationData":[OD(0.0)],"derivedFrom":[makeQuery(id+"F5.opExtrude","SWEPT_FACE",FACE,{"disambiguationData":[OSD([sQuery(id+"F4.wireOp",EDGE,"E30")])]}),makeQuery(id+"F8.opExtrude","SWEPT_FACE",FACE,{"disambiguationData":[OSD([sQuery(id+"F7.wireOp",EDGE,"E67")])]})]});
            fillet(context, id + "F14", {"entities" : qUnion([Q0, Q1, Q2, Q3, Q4, Q5]), "radius" : 3 * mm, "tangentPropagation" : true, "allowEdgeOverflow" : false});
        }
        {
            var Q0;
            Q0=makeQuery(id+"F1.opExtrude","CAP_EDGE",EDGE,{"disambiguationData":[OSD([sQuery(id+"F0.wireOp",EDGE,"E1.bottom")])],"isStart":false});
            fillet(context, id + "F15", {"entities" : qUnion([Q0]), "radius" : 2 * mm, "tangentPropagation" : true, "allowEdgeOverflow" : false});
        }
        {
            var Q0;
            Q0=qCreatedBy(makeId("Top.planeOp"),FACE);
            var sketch = newSketch(context, id + "F16", { "sketchPlane" : qUnion([Q0])});
            skArc(sketch, "E79", {"start": v(11.53, 104.7) * mm, "mid": v(-3.47, 119.7) * mm, "end": v(-18.47, 104.7) * mm});
            skLineSegment(sketch, "E80", {"start": v(-18.47, 104.7) * mm, "end": v(11.53, 104.7) * mm});
            skCircle(sketch, "E81", {"center": v(-3.47, 104.7) * mm, "radius": 6 * mm});
            skLineSegment(sketch, "E82", {"start": v(-36.47, 74.7) * mm, "end": v(29.53, 74.7) * mm});
            skLineSegment(sketch, "E83", {"start": v(-3.47, 74.7) * mm, "end": v(-3.47, 104.7) * mm, "construction": true});
            skLineSegment(sketch, "E84", {"start": v(-18.47, 104.7) * mm, "end": v(-18.47, 92.7) * mm});
            skLineSegment(sketch, "E85", {"start": v(-18.47, 92.7) * mm, "end": v(-36.47, 74.7) * mm});
            skLineSegment(sketch, "E86", {"start": v(11.53, 104.7) * mm, "end": v(11.53, 92.7) * mm});
            skLineSegment(sketch, "E87", {"start": v(11.53, 92.7) * mm, "end": v(29.53, 74.7) * mm});
            skLineSegment(sketch, "E88.MirrorCS", {"start": v(29.53, 74.7) * mm, "end": v(-36.47, 74.7) * mm});
            skArc(sketch, "E89.MirrorCS", {"start": v(-18.47, 104.7) * mm, "mid": v(-3.47, 119.7) * mm, "end": v(11.53, 104.7) * mm});
            skLineSegment(sketch, "E90.MirrorCS", {"start": v(11.53, 104.7) * mm, "end": v(-18.47, 104.7) * mm});
            skLineSegment(sketch, "E91", {"start": v(-74.55, 0) * mm, "end": v(74.16, 0) * mm, "construction": true});
            skLineSegment(sketch, "E92.MirrorCS", {"start": v(11.53, -92.7) * mm, "end": v(29.53, -74.7) * mm});
            skLineSegment(sketch, "E93.MirrorCS", {"start": v(-18.47, -92.7) * mm, "end": v(-36.47, -74.7) * mm});
            skLineSegment(sketch, "E94.MirrorCS", {"start": v(-36.47, -74.7) * mm, "end": v(29.53, -74.7) * mm});
            skCircle(sketch, "E95.MirrorC", {"center": v(-3.47, -104.7) * mm, "radius": 6 * mm});
            skLineSegment(sketch, "E96.MirrorCS", {"start": v(29.53, -74.7) * mm, "end": v(-36.47, -74.7) * mm});
            skLineSegment(sketch, "E97.MirrorCS", {"start": v(-18.47, -104.7) * mm, "end": v(-18.47, -92.7) * mm});
            skArc(sketch, "E98.MirrorCS", {"start": v(11.53, -104.7) * mm, "mid": v(-3.47, -119.7) * mm, "end": v(-18.47, -104.7) * mm});
            skLineSegment(sketch, "E99.MirrorCS", {"start": v(11.53, -104.7) * mm, "end": v(11.53, -92.7) * mm});
            skArc(sketch, "E100.MirrorCS", {"start": v(-18.47, -104.7) * mm, "mid": v(-3.47, -119.7) * mm, "end": v(11.53, -104.7) * mm});
            skLineSegment(sketch, "E101.MirrorCS", {"start": v(-18.47, -104.7) * mm, "end": v(11.53, -104.7) * mm});
            skLineSegment(sketch, "E102.MirrorCS", {"start": v(11.53, -104.7) * mm, "end": v(-18.47, -104.7) * mm});
            skLineSegment(sketch, "E103.MirrorCS", {"start": v(-3.47, -74.7) * mm, "end": v(-3.47, -104.7) * mm, "construction": true});
            skSolve(sketch);
        }
        {
            var Q0;
            Q0=makeQuery(id+"F16.imprint","IMPRINT",FACE,{"disambiguationData":[TD([[makeQuery(id+"F16.imprint","IMPRINT",EDGE,{"derivedFrom":sQuery(id+"F16.wireOp",EDGE,"E87")}),-1.0]])]});
            var Q1;
            {var subQ0=sQuery(id+"F16.wireOp",EDGE,"E79");Q1=makeQuery(id+"F16.imprint","IMPRINT",FACE,{"disambiguationData":[TD([[makeQuery(id+"F16.imprint","IMPRINT",EDGE,{"derivedFrom":subQ0}),1.0]])]});}
            var Q2;
            {var subQ0=sQuery(id+"F16.wireOp",EDGE,"E90.MirrorCS");var subQ1=sQuery(id+"F16.wireOp",EDGE,"E81");var subQ2=makeQuery(id+"F16.imprint","INTERSECT",VERTEX,{"disambiguationData":[OD(0.0)],"derivedFrom":[subQ1,subQ0]});Q2=makeQuery(id+"F16.imprint","IMPRINT",FACE,{"disambiguationData":[TD([[makeQuery(id+"F16.imprint","IMPRINT",EDGE,{"disambiguationData":[TD([[subQ2,1.0]])],"derivedFrom":subQ1}),-1.0]])]});}
            var Q3;
            {var subQ0=sQuery(id+"F16.wireOp",EDGE,"E90.MirrorCS");var subQ1=sQuery(id+"F16.wireOp",EDGE,"E81");var subQ2=makeQuery(id+"F16.imprint","INTERSECT",VERTEX,{"disambiguationData":[OD(0.0)],"derivedFrom":[subQ1,subQ0]});Q3=makeQuery(id+"F16.imprint","IMPRINT",FACE,{"disambiguationData":[TD([[makeQuery(id+"F16.imprint","IMPRINT",EDGE,{"disambiguationData":[TD([[subQ2,-1.0]])],"derivedFrom":subQ1}),-1.0]])]});}
            var Q4;
            {var subQ0=sQuery(id+"F16.wireOp",EDGE,"E100.MirrorCS");Q4=makeQuery(id+"F16.imprint","IMPRINT",FACE,{"disambiguationData":[TD([[makeQuery(id+"F16.imprint","IMPRINT",EDGE,{"derivedFrom":subQ0}),1.0]])]});}
            var Q5;
            {var subQ0=sQuery(id+"F16.wireOp",EDGE,"E95.MirrorC");var subQ1=sQuery(id+"F16.wireOp",EDGE,"E102.MirrorCS");var subQ2=makeQuery(id+"F16.imprint","INTERSECT",VERTEX,{"disambiguationData":[OD(0.0)],"derivedFrom":[subQ1,subQ0]});Q5=makeQuery(id+"F16.imprint","IMPRINT",FACE,{"disambiguationData":[TD([[makeQuery(id+"F16.imprint","IMPRINT",EDGE,{"disambiguationData":[TD([[subQ2,-1.0]])],"derivedFrom":subQ1}),1.0]])]});}
            var Q6;
            {var subQ0=sQuery(id+"F16.wireOp",EDGE,"E95.MirrorC");var subQ1=sQuery(id+"F16.wireOp",EDGE,"E102.MirrorCS");var subQ2=makeQuery(id+"F16.imprint","INTERSECT",VERTEX,{"disambiguationData":[OD(0.0)],"derivedFrom":[subQ1,subQ0]});Q6=makeQuery(id+"F16.imprint","IMPRINT",FACE,{"disambiguationData":[TD([[makeQuery(id+"F16.imprint","IMPRINT",EDGE,{"disambiguationData":[TD([[subQ2,-1.0]])],"derivedFrom":subQ1}),-1.0]])]});}
            var Q7;
            {var subQ5=sQuery(id+"F16.wireOp",EDGE,"E99.MirrorCS");Q7=makeQuery(id+"F16.imprint","IMPRINT",FACE,{"disambiguationData":[TD([[makeQuery(id+"F16.imprint","IMPRINT",EDGE,{"derivedFrom":subQ5}),1.0]])]});}
            extrude(context, id + "F17", {"entities" : qUnion([Q0, Q1, Q2, Q3, Q4, Q5, Q6, Q7]), "oppositeDirection" : true, "depth" : 2 * mm});
        }
    });
